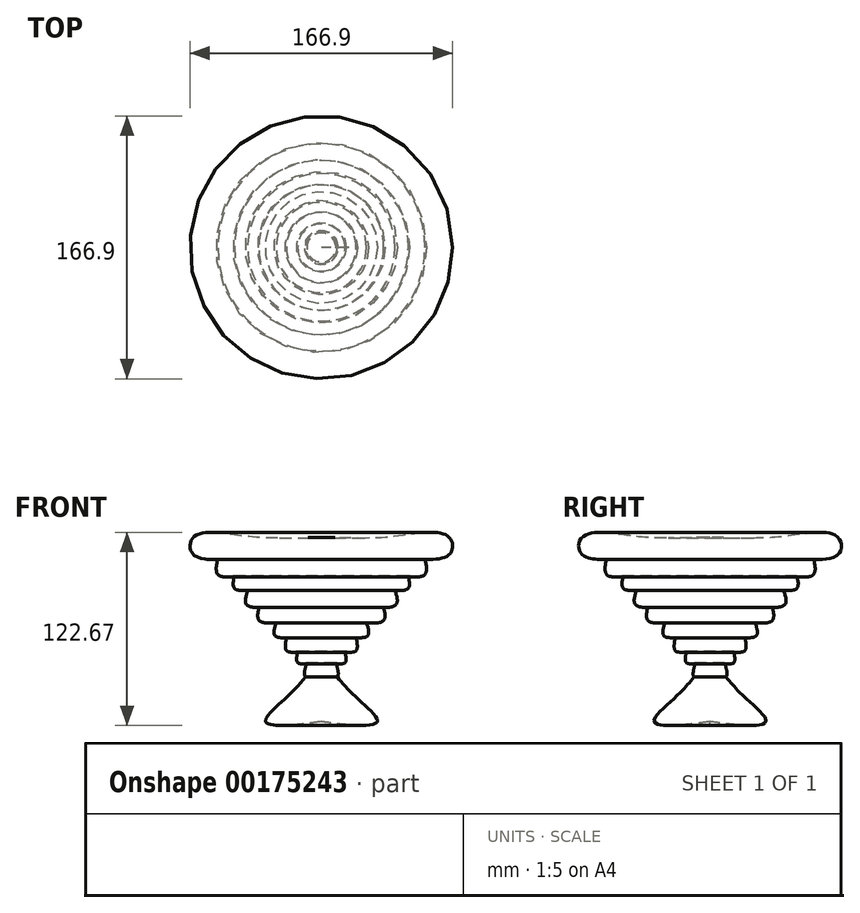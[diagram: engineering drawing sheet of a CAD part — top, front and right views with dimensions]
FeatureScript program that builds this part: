
annotation { "Feature Type Name" : "Feature", "Feature Type Description" : "" }
export const myFeature = defineFeature(function(context is Context, id is Id, definition is map)
    precondition{}
    {
        {
            var Q0;
            Q0=qCreatedBy(makeId("Front.planeOp"),FACE);
            var sketch = newSketch(context, id + "F0", { "sketchPlane" : qUnion([Q0])});
            skFitSpline(sketch, "E0", {"points": [v(0, 56.47) * mm, v(28.87, 56.46) * mm, v(51.28, 58.07) * mm, v(80.8, 57.1) * mm, v(81.04, 45.56) * mm, v(51.85, 43.72) * mm, v(30.83, 43.78) * mm, v(0, 45.86) * mm], "startDerivative": vector(188.36, 5.13) * mm, "endDerivative": vector(-191.9, 9.34) * mm});
            skFitSpline(sketch, "E1", {"points": [v(65.77, 42.71) * mm, v(65.26, 32.63) * mm, v(51.85, 32.63) * mm, v(29.8, 33.82) * mm, v(10.73, 34.12) * mm, v(0, 34.72) * mm], "startDerivative": vector(23.06, -80.44) * mm, "endDerivative": vector(-58.83, 4.02) * mm});
            skFitSpline(sketch, "E2", {"points": [v(55.2, 32.16) * mm, v(54.83, 23.99) * mm, v(37.25, 23.99) * mm, v(18.48, 23.99) * mm, v(0, 24.88) * mm], "startDerivative": vector(11.74, -54.88) * mm, "endDerivative": vector(-68.48, 5.11) * mm});
            skFitSpline(sketch, "E3", {"points": [v(46.8, 23) * mm, v(47.08, 13.56) * mm, v(25.63, 13.56) * mm, v(10.13, 14.45) * mm, v(0, 14.45) * mm], "startDerivative": vector(17.1, -55.31) * mm, "endDerivative": vector(-46.42, -0.19) * mm});
            skFitSpline(sketch, "E4", {"points": [v(39.63, 12.13) * mm, v(39.04, 3.43) * mm, v(17.28, 4.02) * mm, v(0, 3.72) * mm], "startDerivative": vector(9.04, -42.49) * mm, "endDerivative": vector(-43.3, -4.29) * mm});
            skFitSpline(sketch, "E5", {"points": [v(28.64, 2.6) * mm, v(29.2, -6.1) * mm, v(17.28, -6.1) * mm, v(8.05, -5.51) * mm, v(0, -6.7) * mm], "startDerivative": vector(13.82, -45.06) * mm, "endDerivative": vector(-35.15, -6.62) * mm});
            skFitSpline(sketch, "E6", {"points": [v(22.16, -6.82) * mm, v(21.75, -15.64) * mm, v(11.32, -15.05) * mm, v(0, -15.05) * mm], "startDerivative": vector(6.15, -36.2) * mm, "endDerivative": vector(-30.45, -2.62) * mm});
            skFitSpline(sketch, "E7", {"points": [v(15.01, -15.71) * mm, v(14.9, -23.1) * mm, v(7.15, -22.8) * mm, v(0, -23.1) * mm], "startDerivative": vector(5.64, -28.35) * mm, "endDerivative": vector(-20.12, -2.9) * mm});
            skFitSpline(sketch, "E8", {"points": [v(9.23, -23.12) * mm, v(10.13, -32.03) * mm, v(0, -32.33) * mm], "startDerivative": vector(7.07, -22.7) * mm, "endDerivative": vector(-25.2, 4) * mm});
            skFitSpline(sketch, "E9", {"points": [v(10.13, -32.03) * mm, v(22.95, -45.74) * mm, v(35.46, -60.34) * mm, v(14, -62.13) * mm, v(0, -60.35) * mm, v(0, -60.94) * mm], "startDerivative": vector(44.28, -52.65) * mm, "endDerivative": vector(0, -41.43) * mm});
            skFitSpline(sketch, "E10", {"points": [v(4.33, -33.02) * mm, v(17.55, -62.45) * mm], "startDerivative": vector(13.3, -29.5) * mm, "endDerivative": vector(13.3, -29.5) * mm});
            skLineSegment(sketch, "E11", {"start": v(0, 71.07) * mm, "end": v(0, -75.24) * mm});
            skSolve(sketch);
        }
        {
            var Q0;
            {var subQ0=sQuery(id+"F0.wireOp",EDGE,"E11");var subQ1=sQuery(id+"F0.wireOp",EDGE,"E0");var subQ2=makeQuery(id+"F0.imprint","INTERSECT",VERTEX,{"disambiguationData":[OD(0.0)],"derivedFrom":[subQ1,subQ0]});Q0=makeQuery(id+"F0.imprint","IMPRINT",FACE,{"disambiguationData":[TD([[makeQuery(id+"F0.imprint","IMPRINT",EDGE,{"disambiguationData":[TD([[subQ2,-1.0]])],"derivedFrom":subQ1}),-1.0]])]});}
            var Q1;
            {var subQ0=sQuery(id+"F0.wireOp",EDGE,"E11");var subQ1=sQuery(id+"F0.wireOp",EDGE,"E0");var subQ2=makeQuery(id+"F0.imprint","INTERSECT",VERTEX,{"disambiguationData":[OD(1.0)],"derivedFrom":[subQ1,subQ0]});Q1=makeQuery(id+"F0.imprint","IMPRINT",FACE,{"disambiguationData":[TD([[makeQuery(id+"F0.imprint","IMPRINT",EDGE,{"disambiguationData":[TD([[subQ2,1.0]])],"derivedFrom":subQ1}),1.0]])]});}
            var Q2;
            {var subQ0=sQuery(id+"F0.wireOp",EDGE,"E11");var subQ1=sQuery(id+"F0.wireOp",EDGE,"E1");var subQ2=makeQuery(id+"F0.imprint","INTERSECT",VERTEX,{"derivedFrom":[subQ1,subQ0]});Q2=makeQuery(id+"F0.imprint","IMPRINT",FACE,{"disambiguationData":[TD([[makeQuery(id+"F0.imprint","IMPRINT",EDGE,{"disambiguationData":[TD([[subQ2,1.0]])],"derivedFrom":subQ1}),1.0]])]});}
            var Q3;
            {var subQ0=sQuery(id+"F0.wireOp",EDGE,"E11");var subQ1=sQuery(id+"F0.wireOp",EDGE,"E2");var subQ2=makeQuery(id+"F0.imprint","INTERSECT",VERTEX,{"derivedFrom":[subQ1,subQ0]});Q3=makeQuery(id+"F0.imprint","IMPRINT",FACE,{"disambiguationData":[TD([[makeQuery(id+"F0.imprint","IMPRINT",EDGE,{"disambiguationData":[TD([[subQ2,1.0]])],"derivedFrom":subQ1}),1.0]])]});}
            var Q4;
            {var subQ0=sQuery(id+"F0.wireOp",EDGE,"E11");var subQ1=sQuery(id+"F0.wireOp",EDGE,"E3");var subQ2=makeQuery(id+"F0.imprint","INTERSECT",VERTEX,{"derivedFrom":[subQ1,subQ0]});Q4=makeQuery(id+"F0.imprint","IMPRINT",FACE,{"disambiguationData":[TD([[makeQuery(id+"F0.imprint","IMPRINT",EDGE,{"disambiguationData":[TD([[subQ2,1.0]])],"derivedFrom":subQ1}),1.0]])]});}
            var Q5;
            {var subQ0=sQuery(id+"F0.wireOp",EDGE,"E11");var subQ1=sQuery(id+"F0.wireOp",EDGE,"E4");var subQ2=makeQuery(id+"F0.imprint","INTERSECT",VERTEX,{"derivedFrom":[subQ1,subQ0]});Q5=makeQuery(id+"F0.imprint","IMPRINT",FACE,{"disambiguationData":[TD([[makeQuery(id+"F0.imprint","IMPRINT",EDGE,{"disambiguationData":[TD([[subQ2,1.0]])],"derivedFrom":subQ1}),1.0]])]});}
            var Q6;
            {var subQ0=sQuery(id+"F0.wireOp",EDGE,"E11");var subQ1=sQuery(id+"F0.wireOp",EDGE,"E5");var subQ2=makeQuery(id+"F0.imprint","INTERSECT",VERTEX,{"derivedFrom":[subQ1,subQ0]});Q6=makeQuery(id+"F0.imprint","IMPRINT",FACE,{"disambiguationData":[TD([[makeQuery(id+"F0.imprint","IMPRINT",EDGE,{"disambiguationData":[TD([[subQ2,1.0]])],"derivedFrom":subQ1}),1.0]])]});}
            var Q7;
            {var subQ0=sQuery(id+"F0.wireOp",EDGE,"E11");var subQ1=sQuery(id+"F0.wireOp",EDGE,"E6");var subQ2=makeQuery(id+"F0.imprint","INTERSECT",VERTEX,{"derivedFrom":[subQ1,subQ0]});Q7=makeQuery(id+"F0.imprint","IMPRINT",FACE,{"disambiguationData":[TD([[makeQuery(id+"F0.imprint","IMPRINT",EDGE,{"disambiguationData":[TD([[subQ2,1.0]])],"derivedFrom":subQ1}),1.0]])]});}
            var Q8;
            {var subQ0=sQuery(id+"F0.wireOp",EDGE,"E11");var subQ1=sQuery(id+"F0.wireOp",EDGE,"E7");var subQ2=makeQuery(id+"F0.imprint","INTERSECT",VERTEX,{"derivedFrom":[subQ1,subQ0]});Q8=makeQuery(id+"F0.imprint","IMPRINT",FACE,{"disambiguationData":[TD([[makeQuery(id+"F0.imprint","IMPRINT",EDGE,{"disambiguationData":[TD([[subQ2,1.0]])],"derivedFrom":subQ1}),1.0]])]});}
            var Q9;
            {var subQ3=sQuery(id+"F0.wireOp",EDGE,"E9");var subQ5=makeQuery(id+"F0.imprint","IMPRINT",VERTEX,{"derivedFrom":subQ3});Q9=makeQuery(id+"F0.imprint","IMPRINT",FACE,{"disambiguationData":[TD([[makeQuery(id+"F0.imprint","IMPRINT",EDGE,{"disambiguationData":[TD([[subQ5,1.0]])],"derivedFrom":subQ3}),-1.0]])]});}
            var Q10;
            Q10=sQuery(id+"F0.wireOp",EDGE,"E0");
            var Q11;
            Q11=sQuery(id+"F0.wireOp",EDGE,"E1");
            var Q12;
            Q12=sQuery(id+"F0.wireOp",EDGE,"E2");
            var Q13;
            Q13=sQuery(id+"F0.wireOp",EDGE,"E3");
            var Q14;
            Q14=sQuery(id+"F0.wireOp",EDGE,"E4");
            var Q15;
            Q15=sQuery(id+"F0.wireOp",EDGE,"E5");
            var Q16;
            Q16=sQuery(id+"F0.wireOp",EDGE,"E6");
            var Q17;
            Q17=sQuery(id+"F0.wireOp",EDGE,"E7");
            var Q18;
            Q18=sQuery(id+"F0.wireOp",EDGE,"E8");
            var Q19;
            Q19=sQuery(id+"F0.wireOp",EDGE,"E9");
            var Q20;
            Q20=sQuery(id+"F0.wireOp",EDGE,"E10");
            var Q21;
            Q21=sQuery(id+"F0.wireOp",EDGE,"E11");
            revolve(context, id + "F1", {"entities" : qUnion([Q0, Q1, Q2, Q3, Q4, Q5, Q6, Q7, Q8, Q9]), "surfaceEntities" : qUnion([Q10, Q11, Q12, Q13, Q14, Q15, Q16, Q17, Q18, Q19, Q20]), "axis" : qUnion([Q21]), "revolveType" : RevolveType.FULL});
        }
    });
